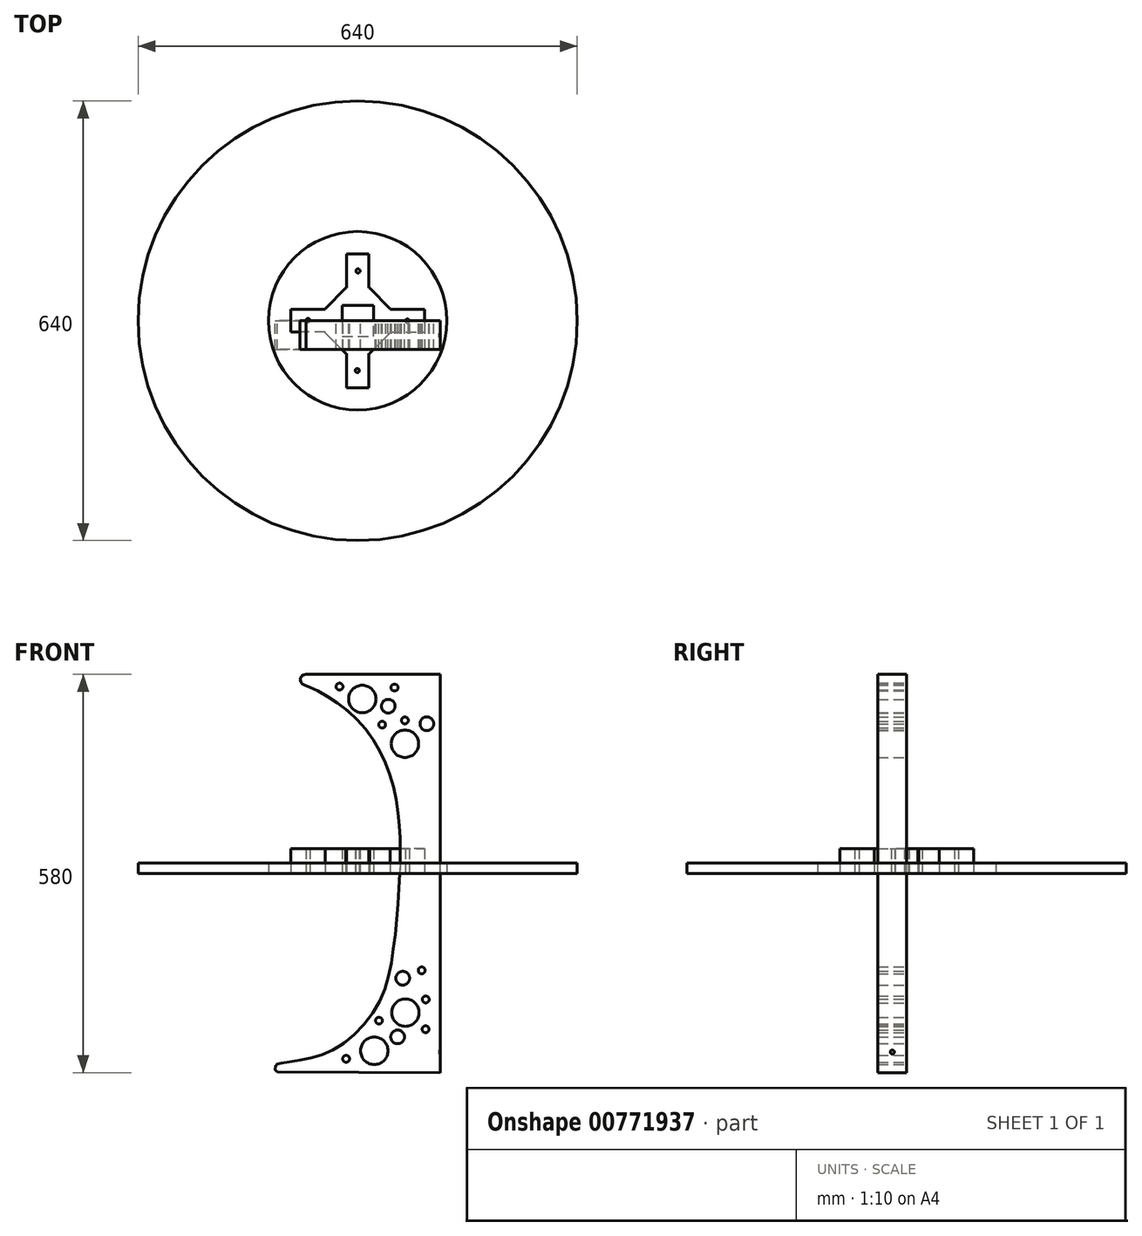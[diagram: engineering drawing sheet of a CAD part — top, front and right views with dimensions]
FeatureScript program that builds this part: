
annotation { "Feature Type Name" : "Feature", "Feature Type Description" : "" }
export const myFeature = defineFeature(function(context is Context, id is Id, definition is map)
    precondition{}
    {
        {
            var Q0;
            Q0=qCreatedBy(makeId("Front.planeOp"),FACE);
            var sketch = newSketch(context, id + "F0", { "sketchPlane" : qUnion([Q0])});
            skLineSegment(sketch, "E0", {"start": v(120.51, 290) * mm, "end": v(-75.49, 289.97) * mm});
            skCircle(sketch, "E1", {"center": v(69.52, -202.7) * mm, "radius": 20 * mm});
            skCircle(sketch, "E2", {"center": v(6.77, 254.1) * mm, "radius": 20 * mm});
            skCircle(sketch, "E3", {"center": v(68.87, 188.92) * mm, "radius": 20 * mm});
            skCircle(sketch, "E4", {"center": v(24.21, -258.22) * mm, "radius": 20 * mm});
            skCircle(sketch, "E5", {"center": v(100.87, 218.02) * mm, "radius": 10 * mm});
            skCircle(sketch, "E6", {"center": v(44.52, 243.63) * mm, "radius": 10 * mm});
            skCircle(sketch, "E7", {"center": v(58.21, -238) * mm, "radius": 10 * mm});
            skCircle(sketch, "E8", {"center": v(65.66, -152.56) * mm, "radius": 10 * mm});
            skCircle(sketch, "E9", {"center": v(31.02, -214.33) * mm, "radius": 5 * mm});
            skCircle(sketch, "E10", {"center": v(98.99, -226.88) * mm, "radius": 5 * mm});
            skCircle(sketch, "E11", {"center": v(99.22, -183.43) * mm, "radius": 5 * mm});
            skCircle(sketch, "E12", {"center": v(93.3, -141.1) * mm, "radius": 5 * mm});
            skCircle(sketch, "E13", {"center": v(68.81, 222.91) * mm, "radius": 5 * mm});
            skCircle(sketch, "E14", {"center": v(35.68, 216.73) * mm, "radius": 5 * mm});
            skCircle(sketch, "E15", {"center": v(-26.46, 272.18) * mm, "radius": 5 * mm});
            skCircle(sketch, "E16", {"center": v(-16.85, -269.95) * mm, "radius": 5 * mm});
            skLineSegment(sketch, "E17", {"start": v(120.28, -290) * mm, "end": v(120.33, -290) * mm});
            skCircle(sketch, "E18", {"center": v(53.68, 270.74) * mm, "radius": 5 * mm});
            skFitSpline(sketch, "E19", {"points": [v(-75.49, 289.97) * mm, v(-81.2, 287.95) * mm, v(-83.78, 281.02) * mm, v(-80.65, 276.04) * mm, v(-74.63, 273.37) * mm, v(-21.5, 242.64) * mm, v(38.23, 166.38) * mm, v(60.75, 70.55) * mm, v(60.16, -23.62) * mm, v(50.69, -119.74) * mm, v(28.77, -192.32) * mm, v(-27.1, -251.96) * mm, v(-80.4, -271.39) * mm, v(-114.37, -276.8) * mm, v(-117.92, -278.15) * mm, v(-120.12, -280.84) * mm, v(-119.95, -286.45) * mm, v(-117.36, -289.12) * mm], "startDerivative": vector(-234.64, -40.15) * mm, "endDerivative": vector(180.93, -109.56) * mm});
            skLineSegment(sketch, "E20", {"start": v(-117.36, -289.12) * mm, "end": v(120.33, -290) * mm});
            skLineSegment(sketch, "E21", {"start": v(120.33, -290) * mm, "end": v(120.51, 290) * mm});
            skSolve(sketch);
        }
        {
            var Q0;
            Q0=makeQuery(id+"F0.imprint","IMPRINT",FACE,{"disambiguationData":[TD([[makeQuery(id+"F0.imprint","IMPRINT",EDGE,{"derivedFrom":sQuery(id+"F0.wireOp",EDGE,"E0")}),1.0]])]});
            extrude(context, id + "F1", {"entities" : qUnion([Q0]), "depth" : 42 * mm, "offsetDistance" : 25 * mm});
        }
        {
            var Q0;
            Q0=qCreatedBy(makeId("Top.planeOp"),FACE);
            var sketch = newSketch(context, id + "F2", { "sketchPlane" : qUnion([Q0])});
            skLineSegment(sketch, "E22", {"start": v(16.5, -97.5) * mm, "end": v(16.5, -47.5) * mm});
            skLineSegment(sketch, "E23", {"start": v(-17.5, -47.5) * mm, "end": v(-47.5, -17.5) * mm});
            skLineSegment(sketch, "E24", {"start": v(-47.5, -16.5) * mm, "end": v(-97.5, -16.5) * mm});
            skLineSegment(sketch, "E25", {"start": v(-97.5, -16.5) * mm, "end": v(-97.5, 16.5) * mm});
            skLineSegment(sketch, "E26", {"start": v(-97.5, 16.5) * mm, "end": v(-47.5, 16.5) * mm});
            skLineSegment(sketch, "E27", {"start": v(16.5, 97.5) * mm, "end": v(16.5, 47.5) * mm});
            skLineSegment(sketch, "E28", {"start": v(-17.5, 47.5) * mm, "end": v(-47.5, 17.5) * mm});
            skLineSegment(sketch, "E29", {"start": v(-16.5, -97.5) * mm, "end": v(-16.5, -47.5) * mm});
            skLineSegment(sketch, "E30", {"start": v(17.5, -47.5) * mm, "end": v(47.5, -17.5) * mm});
            skLineSegment(sketch, "E31", {"start": v(47.5, -16.5) * mm, "end": v(97.5, -16.5) * mm});
            skLineSegment(sketch, "E32", {"start": v(97.5, 16.5) * mm, "end": v(47.5, 16.5) * mm});
            skLineSegment(sketch, "E33", {"start": v(-16.5, 97.5) * mm, "end": v(-16.5, 47.5) * mm});
            skLineSegment(sketch, "E34", {"start": v(17.5, 47.5) * mm, "end": v(47.5, 17.5) * mm});
            skLineSegment(sketch, "E35", {"start": v(16.5, 97.5) * mm, "end": v(-16.5, 97.5) * mm});
            skLineSegment(sketch, "E36", {"start": v(-17.5, 47.5) * mm, "end": v(-16.5, 47.5) * mm});
            skLineSegment(sketch, "E37", {"start": v(17.5, 47.5) * mm, "end": v(16.5, 47.5) * mm});
            skLineSegment(sketch, "E38", {"start": v(-47.5, 16.5) * mm, "end": v(-47.5, 17.5) * mm});
            skLineSegment(sketch, "E39", {"start": v(-47.5, -17.5) * mm, "end": v(-47.5, -16.5) * mm});
            skLineSegment(sketch, "E40", {"start": v(-17.5, -47.5) * mm, "end": v(-16.5, -47.5) * mm});
            skLineSegment(sketch, "E41", {"start": v(16.5, -47.5) * mm, "end": v(17.5, -47.5) * mm});
            skLineSegment(sketch, "E42", {"start": v(16.5, -97.5) * mm, "end": v(-16.5, -97.5) * mm});
            skLineSegment(sketch, "E43", {"start": v(47.5, 16.5) * mm, "end": v(47.5, 17.5) * mm});
            skLineSegment(sketch, "E44", {"start": v(47.5, -17.5) * mm, "end": v(47.5, -16.5) * mm});
            skCircle(sketch, "E45", {"center": v(0.5, 72.5) * mm, "radius": 3 * mm});
            skCircle(sketch, "E46", {"center": v(-0.5, -72.5) * mm, "radius": 3 * mm});
            skCircle(sketch, "E47", {"center": v(72.5, -0.5) * mm, "radius": 3 * mm});
            skCircle(sketch, "E48", {"center": v(-72.5, 0.5) * mm, "radius": 3 * mm});
            skLineSegment(sketch, "E49", {"start": v(-22.5, -22.5) * mm, "end": v(23.5, -22.5) * mm});
            skLineSegment(sketch, "E50", {"start": v(23.5, -22.5) * mm, "end": v(23.5, 22.5) * mm});
            skLineSegment(sketch, "E51", {"start": v(23.5, 22.5) * mm, "end": v(-22.5, 22.5) * mm});
            skLineSegment(sketch, "E52", {"start": v(-22.5, 22.5) * mm, "end": v(-22.5, -22.5) * mm});
            skLineSegment(sketch, "E53", {"start": v(97.5, 16.5) * mm, "end": v(97.5, -16.5) * mm});
            skLineSegment(sketch, "E54", {"start": v(16.5, 97.5) * mm, "end": v(16.5, -97.5) * mm, "construction": true});
            skSolve(sketch);
        }
        {
            var Q0;
            Q0=makeQuery(id+"F2.imprint","IMPRINT",FACE,{"disambiguationData":[TD([[makeQuery(id+"F2.imprint","IMPRINT",EDGE,{"derivedFrom":sQuery(id+"F2.wireOp",EDGE,"E22")}),1.0]])]});
            extrude(context, id + "F3", {"entities" : qUnion([Q0]), "depth" : 36 * mm, "offsetDistance" : 25 * mm});
        }
        {
            var Q0;
            Q0=qCreatedBy(makeId("Top.planeOp"),FACE);
            var sketch = newSketch(context, id + "F4", { "sketchPlane" : qUnion([Q0])});
            skCircle(sketch, "E55", {"center": v(0, 0) * mm, "radius": 130 * mm});
            skCircle(sketch, "E56", {"center": v(0, 0) * mm, "radius": 320 * mm});
            skSolve(sketch);
        }
        {
            var Q0;
            Q0=makeQuery(id+"F4.imprint","IMPRINT",FACE,{"disambiguationData":[TD([[makeQuery(id+"F4.imprint","IMPRINT",EDGE,{"derivedFrom":sQuery(id+"F4.wireOp",EDGE,"E55")}),1.0]])]});
            extrude(context, id + "F5", {"entities" : qUnion([Q0]), "depth" : 15 * mm, "offsetDistance" : 25 * mm});
        }
        {
            var Q0;
            Q0=makeQuery(id+"F4.imprint","IMPRINT",FACE,{"disambiguationData":[TD([[makeQuery(id+"F4.imprint","IMPRINT",EDGE,{"derivedFrom":sQuery(id+"F4.wireOp",EDGE,"E55")}),-1.0]])]});
            extrude(context, id + "F6", {"entities" : qUnion([Q0]), "depth" : 15 * mm, "offsetDistance" : 25 * mm});
        }
        {
            var Q0;
            Q0=makeQuery(id+"F1.opExtrude","SWEPT_FACE",FACE,{"disambiguationData":[OSD([sQuery(id+"F0.wireOp",EDGE,"E21")])]});
            var sketch = newSketch(context, id + "F7", { "sketchPlane" : qUnion([Q0])});
            skPoint(sketch, "E57", {"position": v(-21, -259.96) * mm});
            skPoint(sketch, "E57.positionSnap0", {"position": v(-21, -289.96) * mm});
            skCircle(sketch, "E58", {"center": v(-21, -259.96) * mm, "radius": 3 * mm});
            skSolve(sketch);
        }
        {
            var Q0;
            Q0 = qSketchRegion(id + "F7", true);
            extrude(context, id + "F8", {"entities" : qUnion([Q0]), "operationType" : NewBodyOperationType.REMOVE, "oppositeDirection" : true, "depth" : 2 * mm, "offsetDistance" : 25 * mm});
        }
    });
